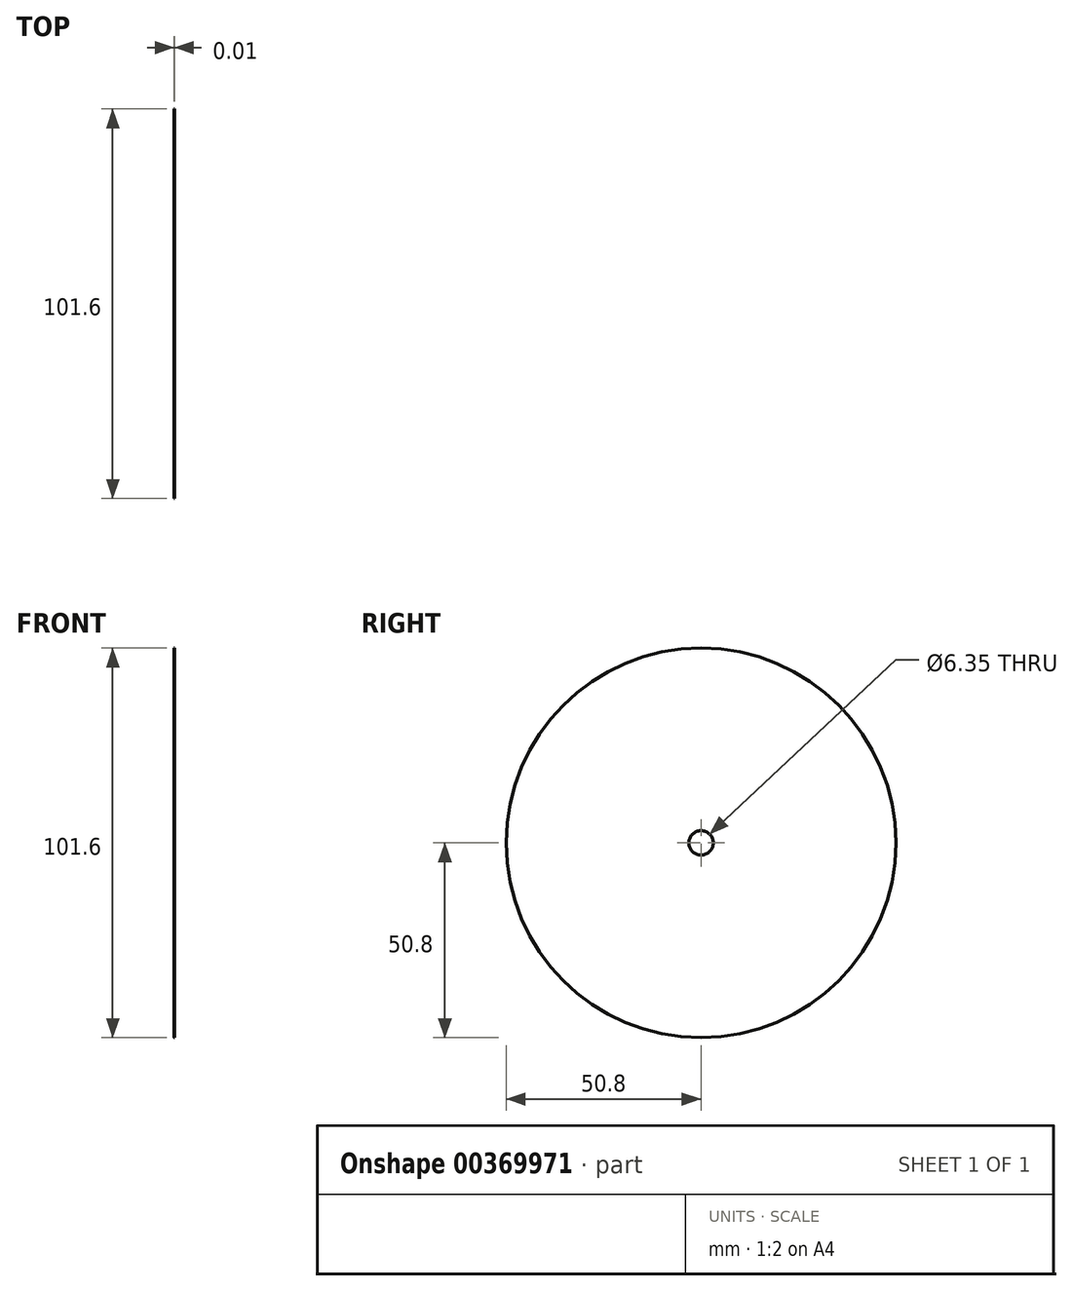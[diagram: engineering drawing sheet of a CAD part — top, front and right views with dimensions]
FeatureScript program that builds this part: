
annotation { "Feature Type Name" : "Feature", "Feature Type Description" : "" }
export const myFeature = defineFeature(function(context is Context, id is Id, definition is map)
    precondition{}
    {
        {
            var Q0;
            Q0=qCreatedBy(makeId("Right.planeOp"),FACE);
            var sketch = newSketch(context, id + "F0", { "sketchPlane" : qUnion([Q0])});
            skCircle(sketch, "E0", {"center": v(0, 0) * mm, "radius": 50.8 * mm});
            skSolve(sketch);
        }
        {
            var Q0;
            Q0=makeQuery(id+"F0.imprint","IMPRINT",FACE,{"disambiguationData":[TD([[makeQuery(id+"F0.imprint","IMPRINT",EDGE,{"derivedFrom":sQuery(id+"F0.wireOp",EDGE,"E0")}),1.0]])]});
            extrude(context, id + "F1", {"entities" : qUnion([Q0]), "depth" : 3 / 406.4 * mm});
        }
        {
            var Q0;
            Q0=qCreatedBy(makeId("Right.planeOp"),FACE);
            var sketch = newSketch(context, id + "F2", { "sketchPlane" : qUnion([Q0])});
            skCircle(sketch, "E1", {"center": v(0, 0) * mm, "radius": 3.18 * mm});
            skSolve(sketch);
        }
        {
            var Q0;
            Q0 = qSketchRegion(id + "F2", true);
            extrude(context, id + "F3", {"entities" : qUnion([Q0]), "operationType" : NewBodyOperationType.REMOVE, "depth" : 0.02 * mm});
        }
    });
